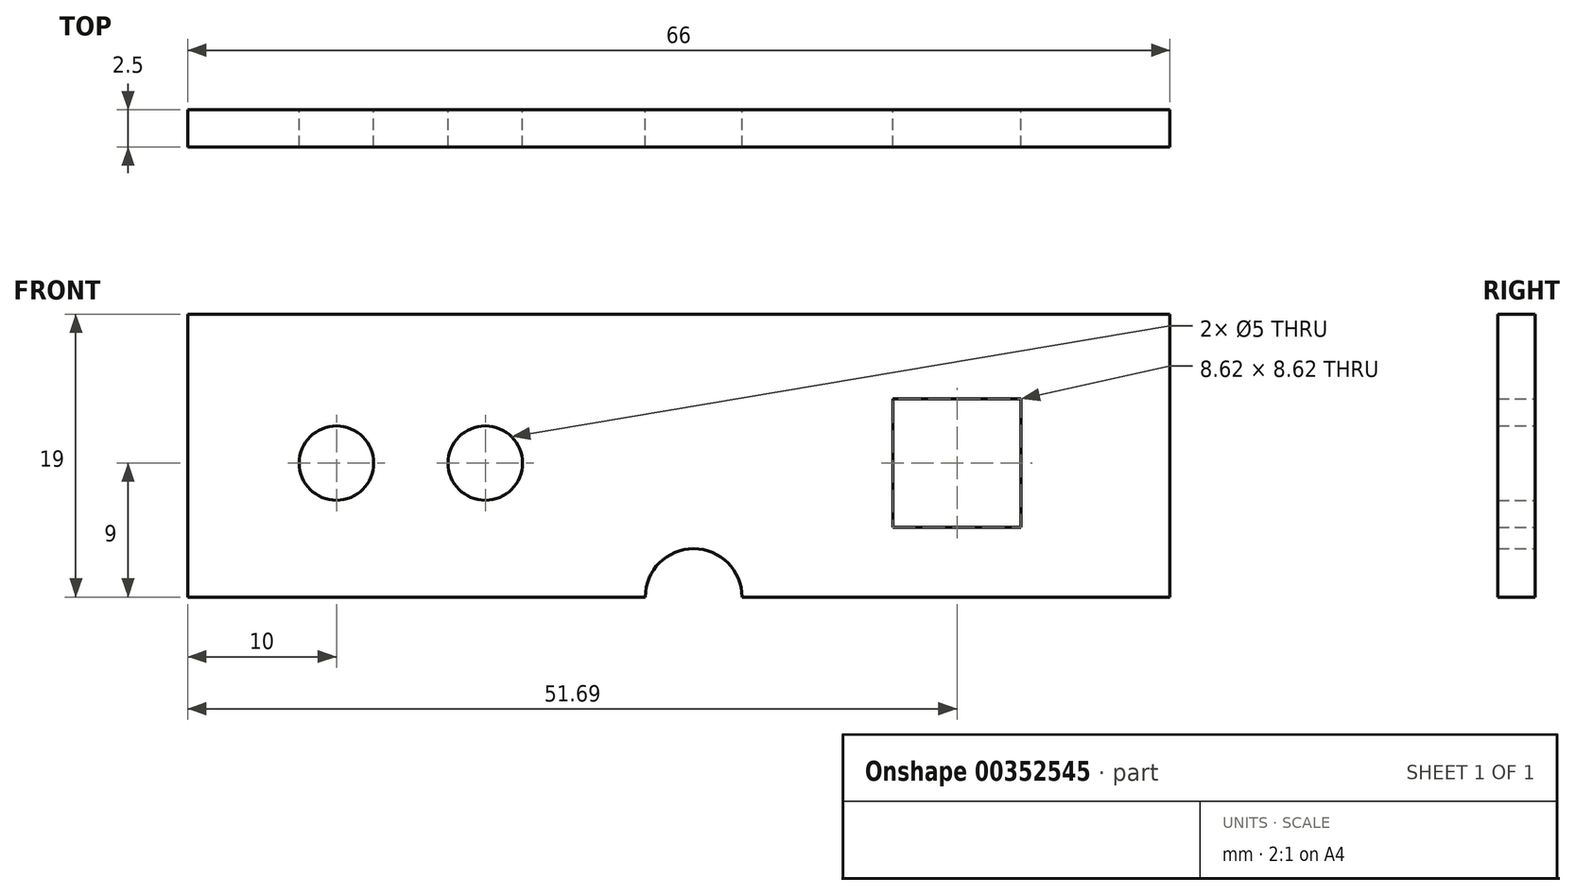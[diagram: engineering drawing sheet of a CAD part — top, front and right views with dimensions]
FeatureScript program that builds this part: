
annotation { "Feature Type Name" : "Feature", "Feature Type Description" : "" }
export const myFeature = defineFeature(function(context is Context, id is Id, definition is map)
    precondition{}
    {
        {
            var Q0;
            Q0=qCreatedBy(makeId("Front.planeOp"),FACE);
            var sketch = newSketch(context, id + "F0", { "sketchPlane" : qUnion([Q0])});
            skLineSegment(sketch, "E0.bottom", {"start": v(-33, 0) * mm, "end": v(-2.25, 0) * mm});
            skLineSegment(sketch, "E0.left", {"start": v(-33, 0) * mm, "end": v(-33, 19) * mm});
            skLineSegment(sketch, "E0.right", {"start": v(33, 0) * mm, "end": v(33, 19) * mm});
            skLineSegment(sketch, "E1", {"start": v(-33, 19) * mm, "end": v(33, 19) * mm});
            skPoint(sketch, "E2", {"position": v(0, 19) * mm});
            skArc(sketch, "E3", {"start": v(4.25, 0) * mm, "mid": v(1, 3.25) * mm, "end": v(-2.25, 0) * mm});
            skLineSegment(sketch, "E4.trimOffspring", {"start": v(4.25, 0) * mm, "end": v(33, 0) * mm});
            skLineSegment(sketch, "E5.bottom", {"start": v(14.38, 13.3) * mm, "end": v(23, 13.3) * mm});
            skLineSegment(sketch, "E5.top", {"start": v(14.38, 4.7) * mm, "end": v(23, 4.7) * mm});
            skLineSegment(sketch, "E5.left", {"start": v(14.38, 13.3) * mm, "end": v(14.38, 4.7) * mm});
            skLineSegment(sketch, "E5.right", {"start": v(23, 13.3) * mm, "end": v(23, 4.7) * mm});
            skCircle(sketch, "E6", {"center": v(-13, 9) * mm, "radius": 2.5 * mm});
            skCircle(sketch, "E7", {"center": v(-23, 9) * mm, "radius": 2.5 * mm});
            skPoint(sketch, "E8", {"position": v(14.38, 9) * mm});
            skSolve(sketch);
        }
        {
            var Q0;
            Q0=qSketchRegion(id+"F0",true);
            extrude(context, id + "F1", {"entities" : qUnion([Q0]), "depth" : 2.5 * mm});
        }
        {
            var Q0;
            Q0 = qSketchRegion(id + "F0", true);
            extrude(context, id + "F2", {"entities" : qUnion([Q0]), "operationType" : NewBodyOperationType.ADD, "depth" : 2.5 * mm});
        }
    });
